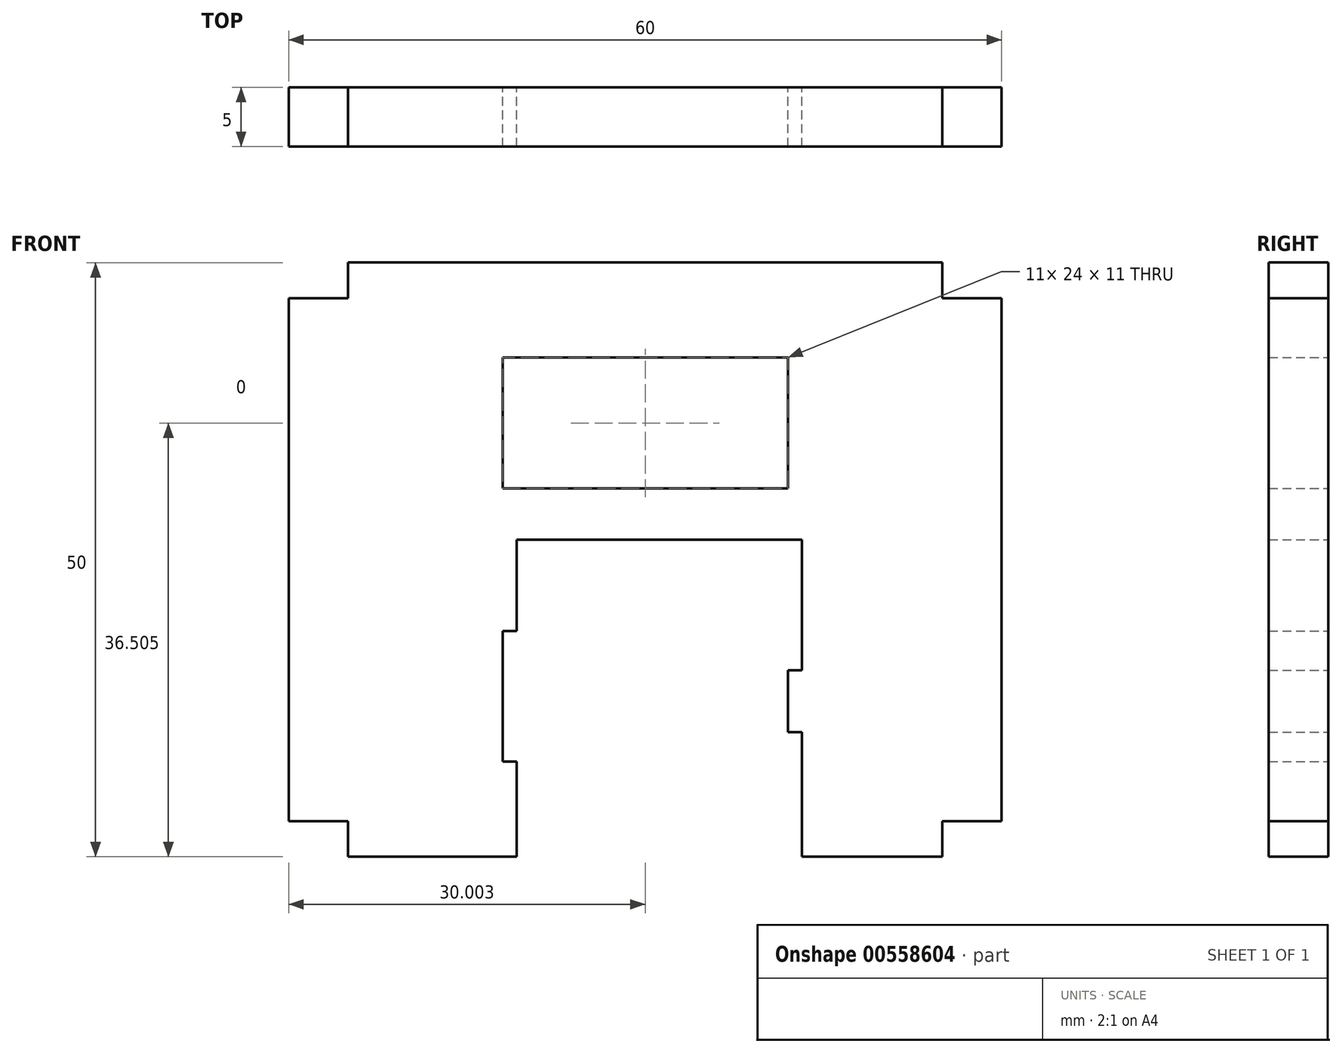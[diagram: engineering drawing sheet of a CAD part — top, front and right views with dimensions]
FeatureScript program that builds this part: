
annotation { "Feature Type Name" : "Feature", "Feature Type Description" : "" }
export const myFeature = defineFeature(function(context is Context, id is Id, definition is map)
    precondition{}
    {
        {
            var Q0;
            Q0=qCreatedBy(makeId("Front.planeOp"),FACE);
            var sketch = newSketch(context, id + "F0", { "sketchPlane" : qUnion([Q0])});
            skLineSegment(sketch, "E0.bottom", {"start": v(-24.13, 46.3) * mm, "end": v(35.87, 46.3) * mm});
            skLineSegment(sketch, "E0.top", {"start": v(-24.13, -3.7) * mm, "end": v(35.87, -3.7) * mm});
            skLineSegment(sketch, "E0.left", {"start": v(-24.13, 46.3) * mm, "end": v(-24.13, -3.7) * mm});
            skLineSegment(sketch, "E0.right", {"start": v(35.87, 46.3) * mm, "end": v(35.87, -3.7) * mm});
            skLineSegment(sketch, "E1", {"start": v(-24.13, 43.3) * mm, "end": v(-19.13, 43.3) * mm});
            skLineSegment(sketch, "E2", {"start": v(35.87, 43.3) * mm, "end": v(30.87, 43.3) * mm});
            skLineSegment(sketch, "E3", {"start": v(30.87, 43.3) * mm, "end": v(30.87, 46.3) * mm});
            skLineSegment(sketch, "E4", {"start": v(-19.13, 43.3) * mm, "end": v(-19.13, 46.3) * mm});
            skLineSegment(sketch, "E5", {"start": v(-19.13, -3.7) * mm, "end": v(-19.13, -0.7) * mm});
            skLineSegment(sketch, "E6", {"start": v(-19.13, -0.7) * mm, "end": v(-24.13, -0.7) * mm});
            skLineSegment(sketch, "E7", {"start": v(30.87, -3.7) * mm, "end": v(30.87, -0.7) * mm});
            skLineSegment(sketch, "E8", {"start": v(30.87, -0.7) * mm, "end": v(35.87, -0.7) * mm});
            skLineSegment(sketch, "E9", {"start": v(5.87, 52.73) * mm, "end": v(5.87, -24.14) * mm, "construction": true});
            skPoint(sketch, "E9.startSnap0", {"position": v(5.87, 46.3) * mm});
            skLineSegment(sketch, "E10", {"start": v(-24.13, 21.3) * mm, "end": v(44.43, 21.3) * mm, "construction": true});
            skLineSegment(sketch, "E11.bottom", {"start": v(-6.13, 38.3) * mm, "end": v(17.87, 38.3) * mm});
            skLineSegment(sketch, "E11.top", {"start": v(-6.13, 27.3) * mm, "end": v(17.87, 27.3) * mm});
            skLineSegment(sketch, "E11.left", {"start": v(-6.13, 38.3) * mm, "end": v(-6.13, 27.3) * mm});
            skLineSegment(sketch, "E11.right", {"start": v(17.87, 38.3) * mm, "end": v(17.87, 27.3) * mm});
            skLineSegment(sketch, "E12", {"start": v(5.87, 38.3) * mm, "end": v(5.87, 27.3) * mm, "construction": true});
            skLineSegment(sketch, "E13.MirrorCS", {"start": v(-6.13, 4.3) * mm, "end": v(17.87, 4.3) * mm});
            skLineSegment(sketch, "E14.MirrorCS", {"start": v(-6.13, 4.3) * mm, "end": v(-6.13, 15.3) * mm});
            skLineSegment(sketch, "E15.MirrorCS", {"start": v(17.87, 4.3) * mm, "end": v(17.87, 15.3) * mm});
            skLineSegment(sketch, "E16.MirrorCS", {"start": v(-6.13, 15.3) * mm, "end": v(17.87, 15.3) * mm});
            skLineSegment(sketch, "E17", {"start": v(-6.13, 32.8) * mm, "end": v(17.87, 32.8) * mm, "construction": true});
            skSolve(sketch);
        }
        {
            var Q0;
            {var subQ4=sQuery(id+"F0.wireOp",EDGE,"E1");Q0=makeQuery(id+"F0.imprint","IMPRINT",FACE,{"disambiguationData":[TD([[makeQuery(id+"F0.imprint","IMPRINT",EDGE,{"derivedFrom":subQ4}),-1.0]])]});}
            var sketch = newSketch(context, id + "F1", { "sketchPlane" : qUnion([Q0])});
            skLineSegment(sketch, "E18.bottom", {"start": v(-4.94, 22.98) * mm, "end": v(19.06, 22.98) * mm});
            skLineSegment(sketch, "E18.top", {"start": v(-4.94, 11.98) * mm, "end": v(19.06, 11.98) * mm});
            skLineSegment(sketch, "E18.left", {"start": v(-4.94, 22.98) * mm, "end": v(-4.94, 11.98) * mm});
            skLineSegment(sketch, "E18.right", {"start": v(19.06, 22.98) * mm, "end": v(19.06, 11.98) * mm});
            skLineSegment(sketch, "E19.bottom", {"start": v(-4.94, 6.8) * mm, "end": v(19.06, 6.8) * mm});
            skLineSegment(sketch, "E19.top", {"start": v(-4.94, -4.2) * mm, "end": v(19.06, -4.2) * mm});
            skLineSegment(sketch, "E19.left", {"start": v(-4.94, 6.8) * mm, "end": v(-4.94, -4.2) * mm});
            skLineSegment(sketch, "E19.right", {"start": v(19.06, 6.8) * mm, "end": v(19.06, -4.2) * mm});
            skLineSegment(sketch, "E20", {"start": v(7.06, 22.98) * mm, "end": v(7.06, -4.2) * mm, "construction": true});
            skSolve(sketch);
        }
        {
            var Q0;
            Q0=makeQuery(id+"F1.imprint","IMPRINT",FACE,{"disambiguationData":[TD([[makeQuery(id+"F1.imprint","IMPRINT",EDGE,{"derivedFrom":sQuery(id+"F1.wireOp",EDGE,"E18.bottom")}),1.0]])]});
            extrude(context, id + "F2", {"entities" : qUnion([Q0]), "depth" : 5 * mm, "offsetDistance" : 25 * mm});
        }
    });
